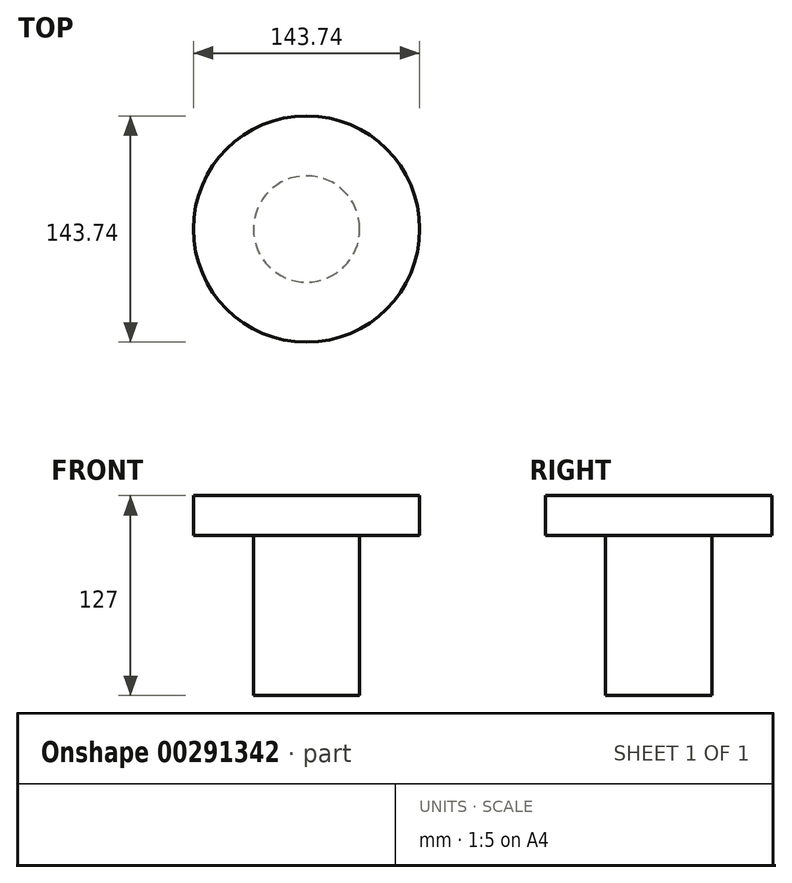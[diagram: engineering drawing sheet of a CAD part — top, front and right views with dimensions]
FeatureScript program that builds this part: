
annotation { "Feature Type Name" : "Feature", "Feature Type Description" : "" }
export const myFeature = defineFeature(function(context is Context, id is Id, definition is map)
    precondition{}
    {
        {
            var Q0;
            Q0=qCreatedBy(makeId("Top.planeOp"),FACE);
            var sketch = newSketch(context, id + "F0", { "sketchPlane" : qUnion([Q0])});
            skCircle(sketch, "E0", {"center": v(0, 0) * mm, "radius": 71.87 * mm});
            skSolve(sketch);
        }
        {
            var Q0;
            Q0 = qSketchRegion(id + "F0", true);
            extrude(context, id + "F1", {"entities" : qUnion([Q0]), "depth" : 25.4 * mm});
        }
        {
            var Q0;
            Q0=makeQuery(id+"F1.opExtrude","CAP_FACE",FACE,{"disambiguationData":[OSD([sQuery(id+"F0.wireOp",EDGE,"E0")])],"isStart":true});
            var sketch = newSketch(context, id + "F2", { "sketchPlane" : qUnion([Q0])});
            skCircle(sketch, "E1", {"center": v(0, 0) * mm, "radius": 33.77 * mm});
            skSolve(sketch);
        }
        {
            var Q0;
            Q0 = qSketchRegion(id + "F2", true);
            extrude(context, id + "F3", {"entities" : qUnion([Q0]), "depth" : 101.6 * mm});
        }
    });
